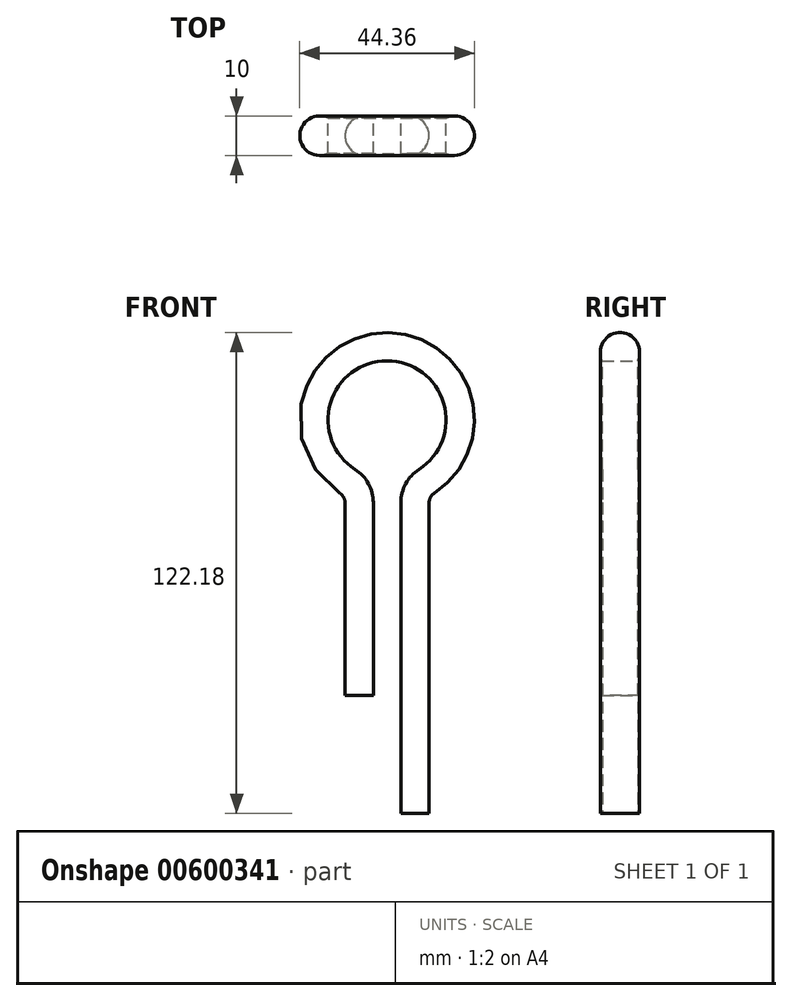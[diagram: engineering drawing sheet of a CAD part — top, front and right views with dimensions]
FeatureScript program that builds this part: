
annotation { "Feature Type Name" : "Feature", "Feature Type Description" : "" }
export const myFeature = defineFeature(function(context is Context, id is Id, definition is map)
    precondition{}
    {
        {
            var Q0;
            Q0=qCreatedBy(makeId("Top.planeOp"),FACE);
            var sketch = newSketch(context, id + "F0", { "sketchPlane" : qUnion([Q0])});
            skArc(sketch, "E0", {"start": v(0, 4.5) * mm, "mid": v(-7.18, 0) * mm, "end": v(0, -4.5) * mm});
            skLineSegment(sketch, "E1", {"start": v(0, -4.5) * mm, "end": v(0, 4.5) * mm});
            skSolve(sketch);
        }
        {
            var Q0;
            Q0=qCreatedBy(makeId("Front.planeOp"),FACE);
            var sketch = newSketch(context, id + "F1", { "sketchPlane" : qUnion([Q0])});
            skLineSegment(sketch, "E2", {"start": v(0, 0) * mm, "end": v(0, 48.96) * mm});
            skLineSegment(sketch, "E3", {"start": v(7, -30) * mm, "end": v(7, 48.96) * mm});
            skArc(sketch, "E4", {"start": v(11.6, 57.38) * mm, "mid": v(3.5, 85) * mm, "end": v(-4.6, 57.38) * mm});
            skPoint(sketch, "E5.visualSharp", {"position": v(0, 55.41) * mm});
            skArc(sketch, "E5.filletArc", {"start": v(0, 48.96) * mm, "mid": v(-1.23, 53.75) * mm, "end": v(-4.6, 57.38) * mm});
            skPoint(sketch, "E6.visualSharp", {"position": v(7, 55.41) * mm});
            skArc(sketch, "E6.filletArc", {"start": v(11.6, 57.38) * mm, "mid": v(8.23, 53.75) * mm, "end": v(7, 48.96) * mm});
            skSolve(sketch);
        }
        {
            var Q0;
            Q0 = qSketchRegion(id + "F0", true);
            var Q1;
            Q1 = qConstructionFilter(qBodyType(qCreatedBy(id + "F1" ,EDGE), BodyType.WIRE), ConstructionObject.NO);
            sweep(context, id + "F2", {"profiles" : qUnion([Q0]), "path" : qUnion([Q1])});
        }
    });
